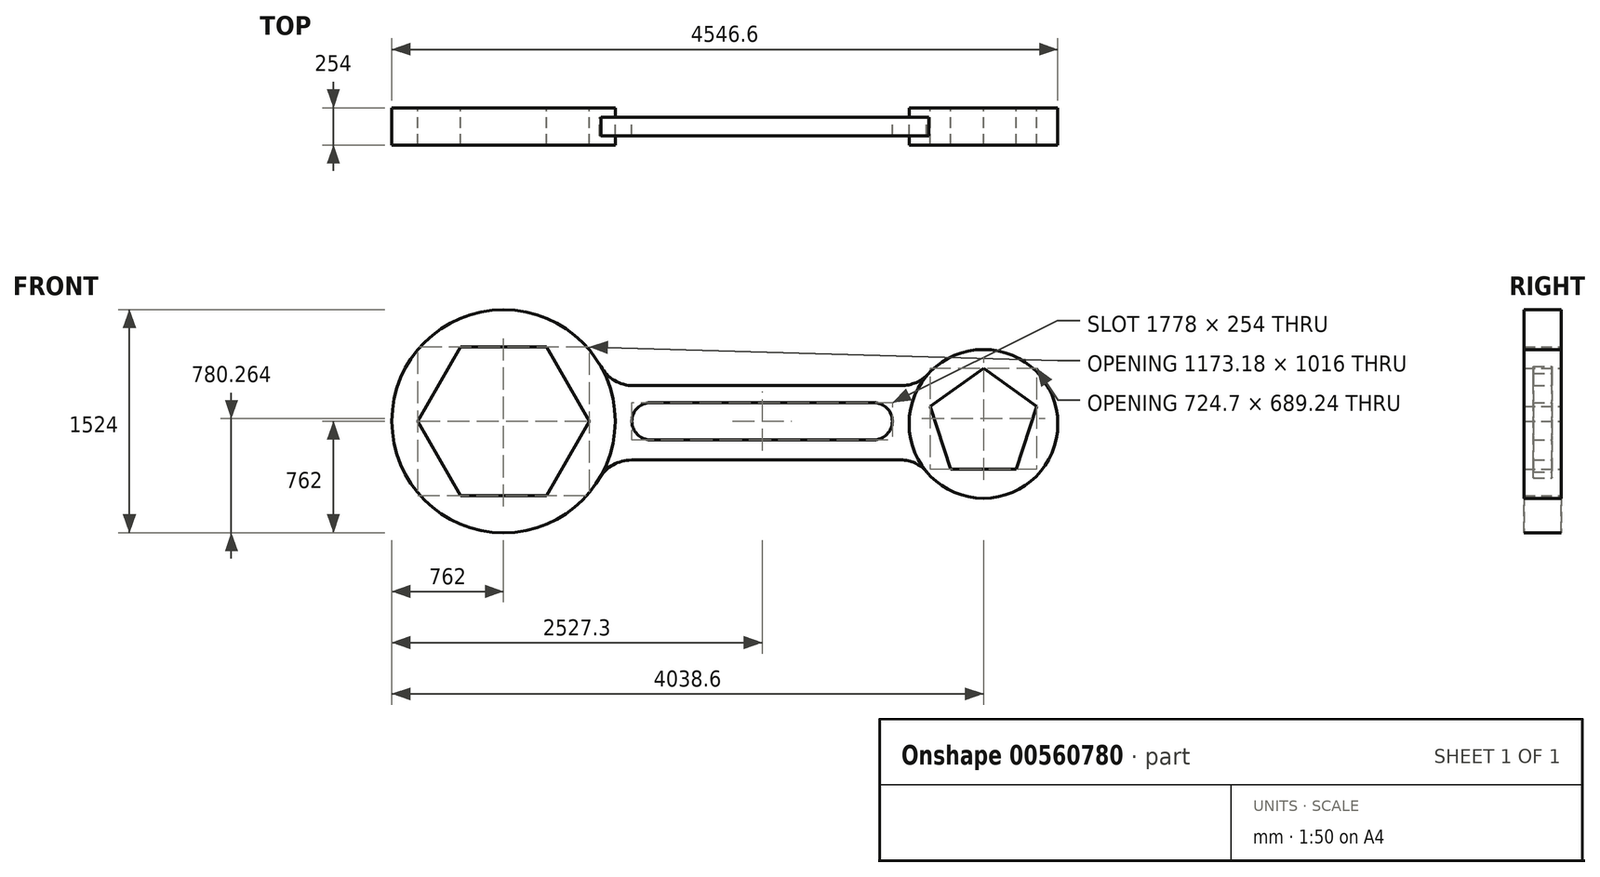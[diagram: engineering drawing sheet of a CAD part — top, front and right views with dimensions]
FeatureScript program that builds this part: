
annotation { "Feature Type Name" : "Feature", "Feature Type Description" : "" }
export const myFeature = defineFeature(function(context is Context, id is Id, definition is map)
    precondition{}
    {
        {
            var Q0;
            Q0=qCreatedBy(makeId("Front.planeOp"),FACE);
            var sketch = newSketch(context, id + "F0", { "sketchPlane" : qUnion([Q0])});
            skCircle(sketch, "E0", {"center": v(0, 0) * mm, "radius": 762 * mm});
            skCircle(sketch, "E1", {"center": v(3276.6, -18.12) * mm, "radius": 508 * mm});
            skLineSegment(sketch, "E2", {"start": v(1765.3, 127) * mm, "end": v(1003.3, 127) * mm});
            skLineSegment(sketch, "E3", {"start": v(1003.3, -127) * mm, "end": v(2527.3, -127) * mm});
            skLineSegment(sketch, "E4", {"start": v(2527.3, 127) * mm, "end": v(1765.3, 127) * mm});
            skArc(sketch, "E5", {"start": v(1003.3, 127) * mm, "mid": v(876.3, 0) * mm, "end": v(1003.3, -127) * mm});
            skArc(sketch, "E6", {"start": v(2527.3, -127) * mm, "mid": v(2654.3, 0) * mm, "end": v(2527.3, 127) * mm});
            skPoint(sketch, "E7.endSnap0", {"position": v(2654.3, 0) * mm});
            skLineSegment(sketch, "E8.0", {"start": v(873.38, -265.1) * mm, "end": v(2714.26, -265.1) * mm});
            skLineSegment(sketch, "E9.0", {"start": v(886.2, 242.9) * mm, "end": v(2715, 242.9) * mm});
            skArc(sketch, "E10", {"start": v(2715, 242.9) * mm, "mid": v(2817.25, 264.4) * mm, "end": v(2902.2, 325.23) * mm});
            skArc(sketch, "E11", {"start": v(873.38, -265.1) * mm, "mid": v(747.78, -298.33) * mm, "end": v(655.04, -389.32) * mm});
            skArc(sketch, "E12", {"start": v(2888.6, -346.02) * mm, "mid": v(2810.36, -286.31) * mm, "end": v(2714.26, -265.1) * mm});
            skArc(sketch, "E13", {"start": v(664.65, 372.68) * mm, "mid": v(757.82, 277.73) * mm, "end": v(886.2, 242.9) * mm});
            skCircle(sketch, "E14.cCircle", {"center": v(0, 0) * mm, "radius": 508 * mm, "construction": true});
            skLineSegment(sketch, "E14.0", {"start": v(-586.59, 0) * mm, "end": v(-293.3, 508) * mm});
            skLineSegment(sketch, "E14.1", {"start": v(-293.3, 508) * mm, "end": v(293.3, 508) * mm});
            skLineSegment(sketch, "E14.2", {"start": v(293.3, 508) * mm, "end": v(586.59, 0) * mm});
            skLineSegment(sketch, "E14.3", {"start": v(586.59, 0) * mm, "end": v(293.3, -508) * mm});
            skLineSegment(sketch, "E14.4", {"start": v(293.3, -508) * mm, "end": v(-293.3, -508) * mm});
            skLineSegment(sketch, "E14.5", {"start": v(-293.3, -508) * mm, "end": v(-586.59, 0) * mm});
            skPoint(sketch, "E14.0.midPoint", {"position": v(-439.94, 254) * mm});
            skCircle(sketch, "E15.cCircle", {"center": v(3276.6, -18.12) * mm, "radius": 308.24 * mm, "construction": true});
            skLineSegment(sketch, "E15.0", {"start": v(3276.6, 362.88) * mm, "end": v(3638.95, 99.62) * mm});
            skLineSegment(sketch, "E15.1", {"start": v(3638.95, 99.62) * mm, "end": v(3500.55, -326.35) * mm});
            skLineSegment(sketch, "E15.2", {"start": v(3500.55, -326.35) * mm, "end": v(3052.65, -326.35) * mm});
            skLineSegment(sketch, "E15.3", {"start": v(3052.65, -326.35) * mm, "end": v(2914.25, 99.62) * mm});
            skLineSegment(sketch, "E15.4", {"start": v(2914.25, 99.62) * mm, "end": v(3276.6, 362.88) * mm});
            skPoint(sketch, "E15.0.midPoint", {"position": v(3457.78, 231.25) * mm});
            skSolve(sketch);
        }
        {
            var Q0;
            Q0=makeQuery(id+"F0.imprint","IMPRINT",FACE,{"disambiguationData":[TD([[makeQuery(id+"F0.imprint","IMPRINT",EDGE,{"derivedFrom":sQuery(id+"F0.wireOp",EDGE,"E14.0")}),1.0]])]});
            var Q1;
            Q1=makeQuery(id+"F0.imprint","IMPRINT",FACE,{"disambiguationData":[TD([[makeQuery(id+"F0.imprint","IMPRINT",EDGE,{"derivedFrom":sQuery(id+"F0.wireOp",EDGE,"E15.0")}),1.0]])]});
            extrude(context, id + "F1", {"entities" : qUnion([Q0, Q1]), "depth" : 254 * mm, "offsetDistance" : 25.4 * mm, "symmetric" : true});
        }
        {
            var Q0;
            Q0=makeQuery(id+"F0.imprint","IMPRINT",FACE,{"disambiguationData":[TD([[makeQuery(id+"F0.imprint","IMPRINT",EDGE,{"derivedFrom":sQuery(id+"F0.wireOp",EDGE,"E2")}),-1.0]])]});
            extrude(context, id + "F2", {"entities" : qUnion([Q0]), "depth" : 127 * mm, "offsetDistance" : 25.4 * mm, "symmetric" : true});
        }
    });
